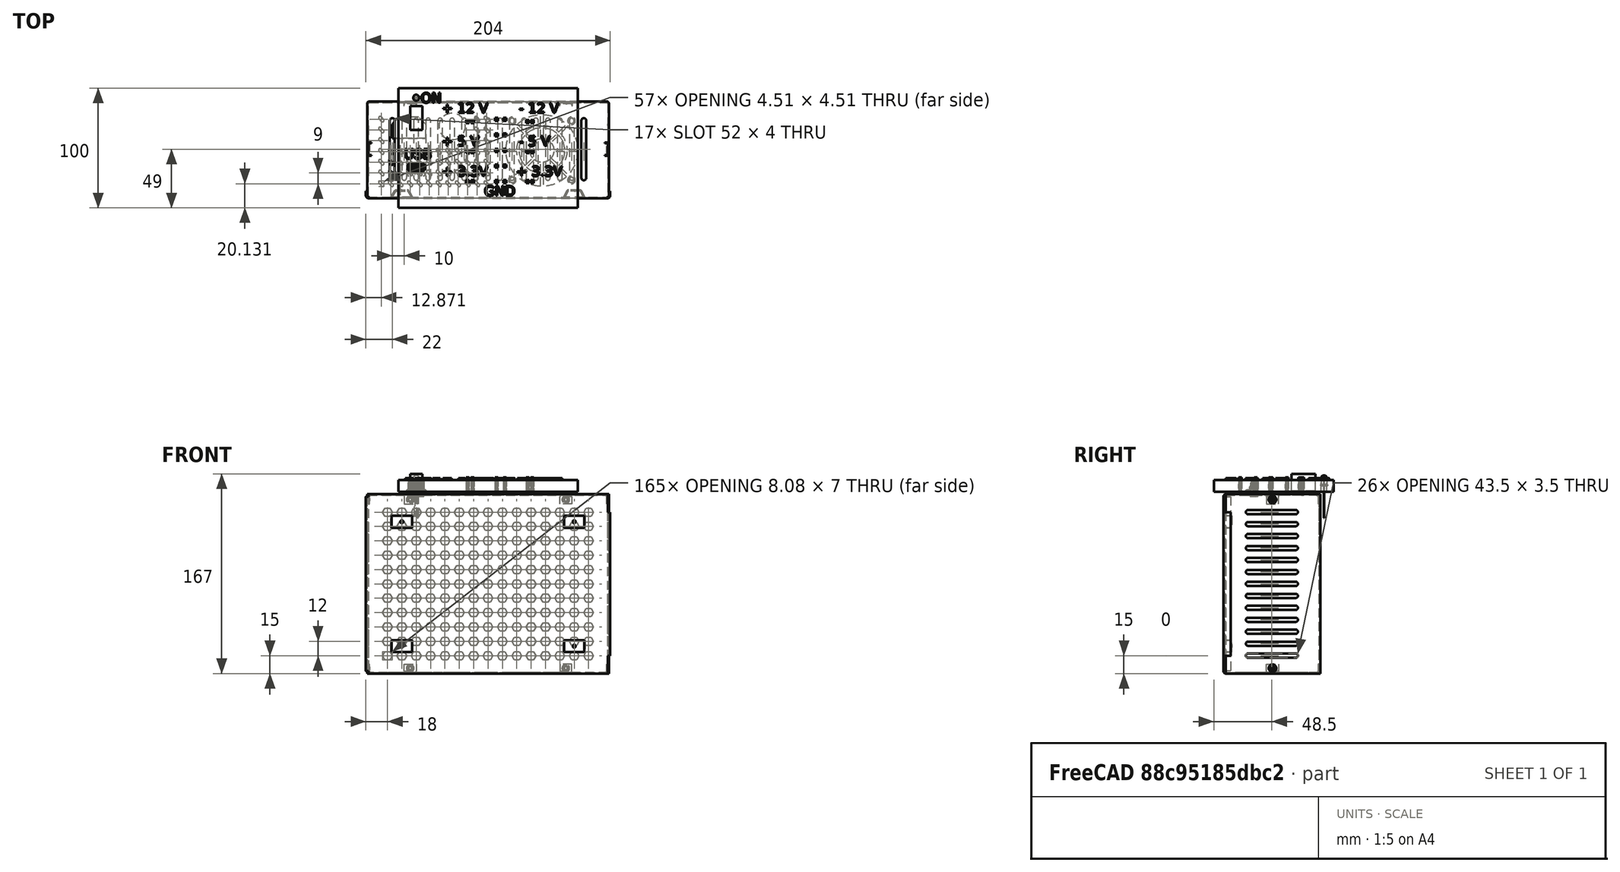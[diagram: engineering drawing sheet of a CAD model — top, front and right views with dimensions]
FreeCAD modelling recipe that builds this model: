
FCSTD DOCUMENT  (FreeCAD 0.18R13588 (Git))
Label: atx_psu
License: All rights reserved
LicenseURL: http://en.wikipedia.org/wiki/All_rights_reserved
objects: Part::Feature×36, Part::Box×26, Part::MultiFuse×13, Part::Extrusion×10, Part::Cut×4, Part::FeaturePython×4, Spreadsheet::Sheet×1, Part::Cylinder×1
note: 94 computed .brp shape members not serialized (recipe doc carries the construction recipe); baked Part::Feature solids carry a one-line shape summary decoded from their .brp

FEATURE [Part::Box] Box  label="Cubo"
  AttacherType = Attacher::AttachEngine3D
  Height = 10
  Length = 150
  Width = 100
  expr: Width = Spreadsheet.alto_psu
  expr: Length = Spreadsheet.ancho_psu
FEATURE [Spreadsheet::Sheet] Spreadsheet
  cells = B3=ancho_psu; C3(ancho_psu)=150; B4=alto_psu; C4(alto_psu)=100; B5=ancho_sw; C5(ancho_sw)=10; B6=alto_sw; C6(alto_sw)=20
FEATURE [Part::Box] Box001  label="switch"
  AttacherType = Attacher::AttachEngine3D
  Height = 14
  Length = 10
  Placement = pos=(10,65,1) rot=(0,0,1;0rad)
  Width = 20
  expr: Width = Spreadsheet.alto_sw
  expr: Length = Spreadsheet.ancho_sw
FEATURE [Part::Feature] Part__Feature  label="femaleUSB"
  Placement = pos=(15,34,10) rot=(1,0,0;4.71239rad)
  shape: bbox 15.79 x 11.14 x 14.45 mm, 375 faces (baked)
FEATURE [Part::Box] Box002  label="Cubo001"
  AttacherType = Attacher::AttachEngine3D
  Height = 24
  Length = 13
  Placement = pos=(8.5,31,-4) rot=(0,0,1;0rad)
  Width = 6
FEATURE [Part::Cut] Cut
  Base = -> Box
  Tool = -> Box002
FEATURE [Part::Feature] Part__Feature001  label="LED 5mm"
  Placement = pos=(15,92,5) rot=(0,0,1;0rad)
  shape: bbox 5.5 x 6 x 35.8 mm, 45 faces, 3 solids (baked)
FEATURE [Part::Feature] Part__Feature003  label="Header001"
  Placement = pos=(50,81,5) rot=(1,0,0;1.5708rad)
  shape: bbox 2.5 x 2.5 x 14.1 mm, 42 faces (baked)
FEATURE [Part::FeaturePython] Array  label="gnd"  # Draft array (typed FeaturePython)
  Angle = 360
  ArrayType = 0
  Axis = (0,0,1)
  Base = -> Part__Feature003
  Center = (0,0,0)
  Fuse = false
  IntervalAxis = (0,0,0)
  IntervalX = (7,0,0)
  IntervalY = (0,13,0)
  IntervalZ = (0,0,0)
  NumberPolar = 1
  NumberX = 2
  NumberY = 5
  NumberZ = 1
  Placement = pos=(32,-59,0) rot=(0,0,1;0rad)
FEATURE [Part::FeaturePython] Array001  label="positive"  # Draft array (typed FeaturePython)
  Angle = 360
  ArrayType = 0
  Axis = (0,0,1)
  Base = -> Part__Feature003
  Center = (0,0,0)
  Fuse = false
  IntervalAxis = (0,0,0)
  IntervalX = (4,0,0)
  IntervalY = (0,25,0)
  IntervalZ = (0,0,0)
  NumberPolar = 1
  NumberX = 2
  NumberY = 3
  NumberZ = 1
  Placement = pos=(8,-59,0) rot=(0,0,1;0rad)
FEATURE [Part::FeaturePython] Array002  label="negative"  # Draft array (typed FeaturePython)
  Angle = 360
  ArrayType = 0
  Axis = (0,0,1)
  Base = -> Part__Feature003
  Center = (0,0,0)
  Fuse = false
  IntervalAxis = (0,0,0)
  IntervalX = (4,0,0)
  IntervalY = (0,25,0)
  IntervalZ = (0,0,0)
  NumberPolar = 1
  NumberX = 2
  NumberY = 3
  NumberZ = 1
  Placement = pos=(58,-59,0) rot=(0,0,1;0rad)
FEATURE [Part::MultiFuse] Fusion  label="outputs_pin"
  Shapes = -> [Array,Array001,Array002]
FEATURE [Part::Box] Box003  label="Cubo002"
  AttacherType = Attacher::AttachEngine3D
  Height = 19
  Length = 2
  Placement = pos=(57,21,-5) rot=(0,0,1;0rad)
  Width = 2
FEATURE [Part::Box] Box004  label="Cubo003"
  AttacherType = Attacher::AttachEngine3D
  Height = 19
  Length = 2
  Placement = pos=(81,73,-5) rot=(0,0,1;0rad)
  Width = 2
FEATURE [Part::Box] Box005  label="Cubo004"
  AttacherType = Attacher::AttachEngine3D
  Height = 19
  Length = 2
  Placement = pos=(61,21,-5) rot=(0,0,1;0rad)
  Width = 2
FEATURE [Part::Box] Box006  label="Cubo005"
  AttacherType = Attacher::AttachEngine3D
  Height = 19
  Length = 2
  Placement = pos=(81,21,-5) rot=(0,0,1;0rad)
  Width = 2
FEATURE [Part::Box] Box007  label="Cubo006"
  AttacherType = Attacher::AttachEngine3D
  Height = 19
  Length = 2
  Placement = pos=(88,21,-5) rot=(0,0,1;0rad)
  Width = 2
FEATURE [Part::Box] Box008  label="Cubo007"
  AttacherType = Attacher::AttachEngine3D
  Height = 19
  Length = 2
  Placement = pos=(107,21,-5) rot=(0,0,1;0rad)
  Width = 2
FEATURE [Part::Box] Box009  label="Cubo008"
  AttacherType = Attacher::AttachEngine3D
  Height = 19
  Length = 2
  Placement = pos=(111,21,-5) rot=(0,0,1;0rad)
  Width = 2
FEATURE [Part::Box] Box010  label="Cubo009"
  AttacherType = Attacher::AttachEngine3D
  Height = 19
  Length = 2
  Placement = pos=(111,46,-5) rot=(0,0,1;0rad)
  Width = 2
FEATURE [Part::Box] Box011  label="Cubo010"
  AttacherType = Attacher::AttachEngine3D
  Height = 19
  Length = 2
  Placement = pos=(107,46,-5) rot=(0,0,1;0rad)
  Width = 2
FEATURE [Part::Box] Box012  label="Cubo011"
  AttacherType = Attacher::AttachEngine3D
  Height = 19
  Length = 2
  Placement = pos=(88,47,-5) rot=(0,0,1;0rad)
  Width = 2
FEATURE [Part::Box] Box013  label="Cubo012"
  AttacherType = Attacher::AttachEngine3D
  Height = 19
  Length = 2
  Placement = pos=(81,47,-5) rot=(0,0,1;0rad)
  Width = 2
FEATURE [Part::Box] Box014  label="Cubo013"
  AttacherType = Attacher::AttachEngine3D
  Height = 19
  Length = 2
  Placement = pos=(81,34,-5) rot=(0,0,1;0rad)
  Width = 2
FEATURE [Part::Box] Box015  label="Cubo014"
  AttacherType = Attacher::AttachEngine3D
  Height = 19
  Length = 2
  Placement = pos=(88,34,-5) rot=(0,0,1;0rad)
  Width = 2
FEATURE [Part::Box] Box016  label="Cubo015"
  AttacherType = Attacher::AttachEngine3D
  Height = 19
  Length = 2
  Placement = pos=(57,46,-5) rot=(0,0,1;0rad)
  Width = 2
FEATURE [Part::Box] Box017  label="Cubo016"
  AttacherType = Attacher::AttachEngine3D
  Height = 19
  Length = 2
  Placement = pos=(61,46,-5) rot=(0,0,1;0rad)
  Width = 2
FEATURE [Part::Box] Box018  label="Cubo017"
  AttacherType = Attacher::AttachEngine3D
  Height = 19
  Length = 2
  Placement = pos=(61,71,-5) rot=(0,0,1;0rad)
  Width = 2
FEATURE [Part::Box] Box019  label="Cubo018"
  AttacherType = Attacher::AttachEngine3D
  Height = 19
  Length = 2
  Placement = pos=(57,71,-5) rot=(0,0,1;0rad)
  Width = 2
FEATURE [Part::Box] Box020  label="Cubo019"
  AttacherType = Attacher::AttachEngine3D
  Height = 19
  Length = 2
  Placement = pos=(111,71,-5) rot=(0,0,1;0rad)
  Width = 2
FEATURE [Part::Box] Box021  label="Cubo020"
  AttacherType = Attacher::AttachEngine3D
  Height = 19
  Length = 2
  Placement = pos=(107,71,-5) rot=(0,0,1;0rad)
  Width = 2
FEATURE [Part::Box] Box022  label="Cubo021"
  AttacherType = Attacher::AttachEngine3D
  Height = 19
  Length = 2
  Placement = pos=(88,73,-5) rot=(0,0,1;0rad)
  Width = 2
FEATURE [Part::Box] Box023  label="Cubo022"
  AttacherType = Attacher::AttachEngine3D
  Height = 19
  Length = 2
  Placement = pos=(88,60,-5) rot=(0,0,1;0rad)
  Width = 2
FEATURE [Part::Box] Box024  label="Cubo023"
  AttacherType = Attacher::AttachEngine3D
  Height = 19
  Length = 2
  Placement = pos=(81,60,-5) rot=(0,0,1;0rad)
  Width = 2
FEATURE [Part::MultiFuse] Fusion001  label="outputs"
  Shapes = -> [Box003,Box018,Box009,Box012,Box016,Box011,Box019,Box020,Box013,Box014,Box010,Box021,Box015,Box017,Box023,Box007,Box006,Box008,Box004,Box005,Box022,Box024]
FEATURE [Part::Cut] Cut001
  Base = -> Cut
  Tool = -> Fusion001
FEATURE [Part::Box] Box025  label="switch001"
  AttacherType = Attacher::AttachEngine3D
  Height = 14
  Length = 10
  Placement = pos=(10,65,-2) rot=(0,0,1;0rad)
  Width = 20
  expr: Width = Spreadsheet.alto_sw
  expr: Length = Spreadsheet.ancho_sw
FEATURE [Part::Cut] Cut002
  Base = -> Cut001
  Tool = -> Box025
FEATURE [Part::Cylinder] Cylinder  label="Cilindro"
  Angle = 360
  AttacherType = Attacher::AttachEngine3D
  Height = 14
  Placement = pos=(15,92,-1) rot=(0,0,1;0rad)
  Radius = 2.5
FEATURE [Part::Cut] Cut003
  Base = -> Cut002
  Tool = -> Cylinder
FEATURE [Part::Feature] Part__Feature025  label="Part007"
  shape: bbox 204 x 80 x 150 mm, 681 faces (baked)
FEATURE [Part::Feature] Part__Feature026  label="Part008"
  Placement = pos=(0,81,0) rot=(0,0,1;0rad)
  shape: bbox 202 x 79 x 150 mm, 1158 faces (baked)
FEATURE [Part::MultiFuse] Fusion002  label="psu"
  Placement = pos=(75,8,-77) rot=(0,0,1;0rad)
  Shapes = -> [Part__Feature025,Part__Feature026]
FEATURE [Part::Feature] path3372
  shape: bbox 7.067 x 7.078 x 2e-07 mm, 0 faces, 0 solids (baked)
FEATURE [Part::Feature] path3374
  shape: bbox 5.325 x 8.389 x 2e-07 mm, 0 faces, 0 solids (baked)
FEATURE [Part::Feature] path3376
  shape: bbox 7.541 x 8.23 x 2e-07 mm, 0 faces, 0 solids (baked)
FEATURE [Part::MultiFuse] Fusion003
  Shapes = -> [path3372,path3374,path3376]
FEATURE [Part::Extrusion] Extrude  label="+5v"
  Base = -> Fusion003
  Dir = (0,0,1)
  DirMode = 2
  FaceMakerClass = Part::FaceMakerBullseye
  LengthFwd = 10
  LengthRev = 0
  Placement = pos=(4,102,11) rot=(0,0,1;0rad)
  Solid = true
  Symmetric = false
FEATURE [Part::Feature] path3423
  shape: bbox 7.067 x 7.078 x 2e-07 mm, 0 faces, 0 solids (baked)
FEATURE [Part::Feature] path3425
  shape: bbox 5.418 x 8.538 x 2e-07 mm, 0 faces, 0 solids (baked)
FEATURE [Part::Feature] path3427
  shape: bbox 1.163 x 1.4 x 2e-07 mm, 0 faces, 0 solids (baked)
FEATURE [Part::Feature] path3429
  shape: bbox 5.418 x 8.538 x 2e-07 mm, 0 faces, 0 solids (baked)
FEATURE [Part::Feature] path3431
  shape: bbox 7.541 x 8.23 x 2e-07 mm, 0 faces, 0 solids (baked)
FEATURE [Part::Feature] path3433
  shape: bbox 7.067 x 7.078 x 2e-07 mm, 0 faces, 0 solids (baked)
FEATURE [Part::Feature] path3435
  shape: bbox 4.9 x 8.23 x 2e-07 mm, 0 faces, 0 solids (baked)
FEATURE [Part::Feature] path3437
  shape: bbox 5.226 x 8.378 x 2e-07 mm, 0 faces, 0 solids (baked)
FEATURE [Part::Feature] path3439
  shape: bbox 7.541 x 8.23 x 2e-07 mm, 0 faces, 0 solids (baked)
FEATURE [Part::Feature] path3441
  shape: bbox 2.971 x 0.904 x 2e-07 mm, 0 faces, 0 solids (baked)
FEATURE [Part::Feature] path3443
  shape: bbox 4.9 x 8.23 x 2e-07 mm, 0 faces, 0 solids (baked)
FEATURE [Part::Feature] path3445
  shape: bbox 5.226 x 8.378 x 2e-07 mm, 0 faces, 0 solids (baked)
FEATURE [Part::Feature] path3447
  shape: bbox 7.541 x 8.23 x 2e-07 mm, 0 faces, 0 solids (baked)
FEATURE [Part::Feature] path3449
  shape: bbox 2.971 x 0.904 x 2e-07 mm, 0 faces, 0 solids (baked)
FEATURE [Part::Feature] path3451
  shape: bbox 5.325 x 8.389 x 2e-07 mm, 0 faces, 0 solids (baked)
FEATURE [Part::Feature] path3453
  shape: bbox 7.541 x 8.23 x 2e-07 mm, 0 faces, 0 solids (baked)
FEATURE [Part::Feature] path3455
  shape: bbox 7.188 x 8.538 x 2e-07 mm, 0 faces, 0 solids (baked)
FEATURE [Part::Feature] path3457
  shape: bbox 6.229 x 8.23 x 2e-07 mm, 0 faces, 0 solids (baked)
FEATURE [Part::Feature] path3459
  shape: bbox 4.63 x 6.4 x 2e-07 mm, 0 faces, 0 solids (baked)
FEATURE [Part::Feature] path3459001
  shape: bbox 6.918 x 8.23 x 2e-07 mm, 0 faces, 0 solids (baked)
FEATURE [Part::Feature] path3461
  shape: bbox 6.3 x 8.389 x 2e-07 mm, 0 faces, 0 solids (baked)
FEATURE [Part::Feature] path3463
  shape: bbox 5.793 x 8.538 x 2e-07 mm, 0 faces, 0 solids (baked)
FEATURE [Part::Feature] path3465
  shape: bbox 3.55 x 3.015 x 2e-07 mm, 0 faces, 0 solids (baked)
FEATURE [Part::Feature] path3465001
  shape: bbox 3.263 x 2.48 x 2e-07 mm, 0 faces, 0 solids (baked)
FEATURE [Part::Feature] path3465002
  shape: bbox 5.837 x 8.23 x 2e-07 mm, 0 faces, 0 solids (baked)
FEATURE [Part::Feature] path3475
  shape: bbox 5.27 x 6.73 x 2e-07 mm, 0 faces, 0 solids (baked)
FEATURE [Part::Feature] path3475001
  shape: bbox 7.618 x 8.538 x 2e-07 mm, 0 faces, 0 solids (baked)
FEATURE [Part::Feature] path3477
  shape: bbox 6.229 x 8.23 x 2e-07 mm, 0 faces, 0 solids (baked)
FEATURE [Part::MultiFuse] Fusion004
  Shapes = -> [path3423,path3425,path3427,path3429,path3431]
FEATURE [Part::MultiFuse] Fusion005
  Shapes = -> [path3433,path3435,path3437,path3439]
FEATURE [Part::MultiFuse] Fusion006
  Shapes = -> [path3441,path3443,path3445,path3447]
FEATURE [Part::MultiFuse] Fusion007
  Shapes = -> [path3449,path3451,path3453]
FEATURE [Part::MultiFuse] Fusion008
  Shapes = -> [path3459,path3457,path3455,path3459001]
FEATURE [Part::MultiFuse] Fusion010
  Shapes = -> [path3475,path3475001,path3477]
FEATURE [Part::Extrusion] Extrude001  label="+3.3v"
  Base = -> Fusion004
  Dir = (0,0,1)
  DirMode = 2
  FaceMakerClass = Part::FaceMakerBullseye
  LengthFwd = 10
  LengthRev = 0
  Placement = pos=(61.5,92,11) rot=(0,0,1;0rad)
  Solid = true
  Symmetric = false
FEATURE [Part::Extrusion] Extrude002  label="+12v"
  Base = -> Fusion005
  Dir = (0,0,1)
  DirMode = 2
  FaceMakerClass = Part::FaceMakerBullseye
  LengthFwd = 10
  LengthRev = 0
  Placement = pos=(-0.5,159,11) rot=(0,0,1;0rad)
  Solid = true
  Symmetric = false
FEATURE [Part::Extrusion] Extrude003  label="-12v"
  Base = -> Fusion006
  Dir = (0,0,1)
  DirMode = 2
  FaceMakerClass = Part::FaceMakerBullseye
  LengthFwd = 10
  LengthRev = 0
  Placement = pos=(64,173,11) rot=(0,0,1;0rad)
  Solid = true
  Symmetric = false
FEATURE [Part::Extrusion] Extrude004  label="-5v"
  Base = -> Fusion007
  Dir = (0,0,1)
  DirMode = 2
  FaceMakerClass = Part::FaceMakerBullseye
  LengthFwd = 10
  LengthRev = 0
  Placement = pos=(64,159.5,11) rot=(0,0,1;0rad)
  Solid = true
  Symmetric = false
FEATURE [Part::Extrusion] Extrude005  label="GND"
  Base = -> Fusion008
  Dir = (0,0,1)
  DirMode = 2
  FaceMakerClass = Part::FaceMakerBullseye
  LengthFwd = 10
  LengthRev = 0
  Placement = pos=(35,132,11) rot=(0,0,1;0rad)
  Solid = true
  Symmetric = false
FEATURE [Part::Extrusion] Extrude007  label="ON"
  Base = -> Fusion010
  Dir = (0,0,1)
  DirMode = 2
  FaceMakerClass = Part::FaceMakerBullseye
  LengthFwd = 10
  LengthRev = 0
  Placement = pos=(-18,238,11) rot=(0,0,1;0rad)
  Solid = true
  Symmetric = false
FEATURE [Part::Extrusion] Extrude008  label="+3.3v001"
  Base = -> Fusion004
  Dir = (0,0,1)
  DirMode = 2
  FaceMakerClass = Part::FaceMakerBullseye
  LengthFwd = 10
  LengthRev = 0
  Placement = pos=(-0.5,92,11) rot=(0,0,1;0rad)
  Solid = true
  Symmetric = false
FEATURE [Part::MultiFuse] Fusion011
  Shapes = -> [path3461,path3463,path3465,path3465001,path3465002]
FEATURE [Part::Extrusion] Extrude009  label="USB"
  Base = -> Fusion011
  Dir = (0,0,1)
  DirMode = 2
  FaceMakerClass = Part::FaceMakerBullseye
  LengthFwd = 10
  LengthRev = 0
  Placement = pos=(-32,177,11) rot=(0,0,1;0rad)
  Solid = true
  Symmetric = false
FEATURE [Part::Extrusion] Extrude010  label="+3.3v002"
  Base = -> Fusion004
  Dir = (0,0,1)
  DirMode = 2
  FaceMakerClass = Part::FaceMakerBullseye
  LengthFwd = 10
  LengthRev = 0
  Placement = pos=(-0.5,92,11) rot=(0,0,1;0rad)
  Solid = true
  Symmetric = false
FEATURE [Part::MultiFuse] Fusion012  label="labels"
  Placement = pos=(0,0,-4) rot=(0,0,1;0rad)
  Shapes = -> [Extrude,Extrude003,Extrude009,Extrude007,Extrude008,Extrude010,Extrude001,Extrude002,Extrude004,Extrude005]
FEATURE [Part::FeaturePython] Clone  label="labels001"  # Draft clone (typed FeaturePython)
  AttacherType = Attacher::AttachEngine3D
  Fuse = false
  Objects = -> [Fusion012]
  Placement = pos=(0,0,1) rot=(0,0,1;0rad)
  Scale = (1,1,0.5)
FEATURE [Part::MultiFuse] Fusion013
  Shapes = -> [Cut003,Clone]
